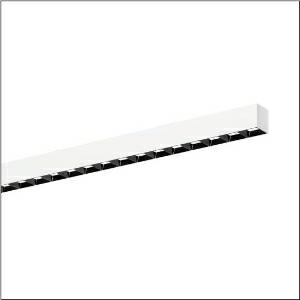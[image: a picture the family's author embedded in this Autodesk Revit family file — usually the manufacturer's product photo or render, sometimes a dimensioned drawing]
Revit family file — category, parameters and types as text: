
# Revit family: silica_r__21_51mx21da34wb_4769
name_source: partatom
category: Lighting Fixtures
units: mm (PartAtom-declared; Revit-internal decimal feet)

## family parameters
Cut with Voids When Loaded = No
Host = Face
Light Source = No
Part Type = Normal
Room Calculation Point = No
Round Connector Dimension = Use Diameter
Shared = No

## types (1)
- --- (1 x LED, 4320 lm, 27.4 W, 3000K)
    Apparent Load = 27 VA
    CIE Flux Codes = 87 99 100 100 100
    Color Rendering = 80
    Color Temperature = 3000K
    Default Elevation = 1800 mm
    Description = Silica® 21, office luminaire, primary light control with darklight reflector, of PMMA, black, CAT 2 (L<= 3000cd/m²), light emission: direct distribution, primary light characteristic: symmetric, installation type: surface-mounted, LED, rated luminous flux: 4.320lm, luminous efficacy: 158lm/W, light colour: 830, colour temperature: 3000K, control gear: DALI 2, with terminal, 3+2-pole, max. 2.5mm², mains connection: 220..240V, AC, 50/60Hz, rated input power: 27.4W, luminaire housing, of aluminium, traffic white (RAL 9016), length: 1.204mm, width: 53mm, height: 53mm, protection rating (complete): IP20, insulation class (complete): insulation class I (protective earthing), certification: CE, permissible operating ambient temperature: 0..+35°C, standard: EN 50419, packaging unit: 1 piece
    Height = 53 mm
    Lamp = 1 x LED
    Lamp Light Flux = 4320 lm
    Lamp Power = 27.4 W
    Lamp count = 1
    Length = 1204 mm
    Luminous efficacy = 158 lm/W
    Manufacturer = Siteco
    ModVariant = No
    Model = 51MX21DA34WB
    Mounting Place = Ceiling
    Mounting Type = Surface mounted
    Number of Poles = 1
    OnlyDefault = Yes
    Power Factor = 1
    Product Name = Silica® 21
    Product group = office luminaire | ceiling mounted
    ProductGroupID = 303
    Protection Class = Protection class I
    Protection Degree = IP 20
    RLX_Detail_Level = 1
    RLX_Emergency_Light_Flux = 0 lm
    RLX_Emergency_Type = 0
    RLX_Emergency_Type_DB = No
    RlxData = <blob elided: 41237 chars, md5=a3db055b>
    Socket = socket
    Standby Power = 0 W
    System Light Flux = 4320 lm
    System Power = 27 W
    Type Comments = factory setting: luminous flux: 100 % | dim-lin: 254 | 393 mA
    Type Image = l_1335873.jpg
    URL = http://relux.com
    VarID = @adj_027455
    Voltage = 0 V
    Weight = 0.00 kg
    Width = 53 mm

## geometry (parser evidence)
native form markers: Blend x4, Sweep x10
no freeform markers — native parametric forms only
